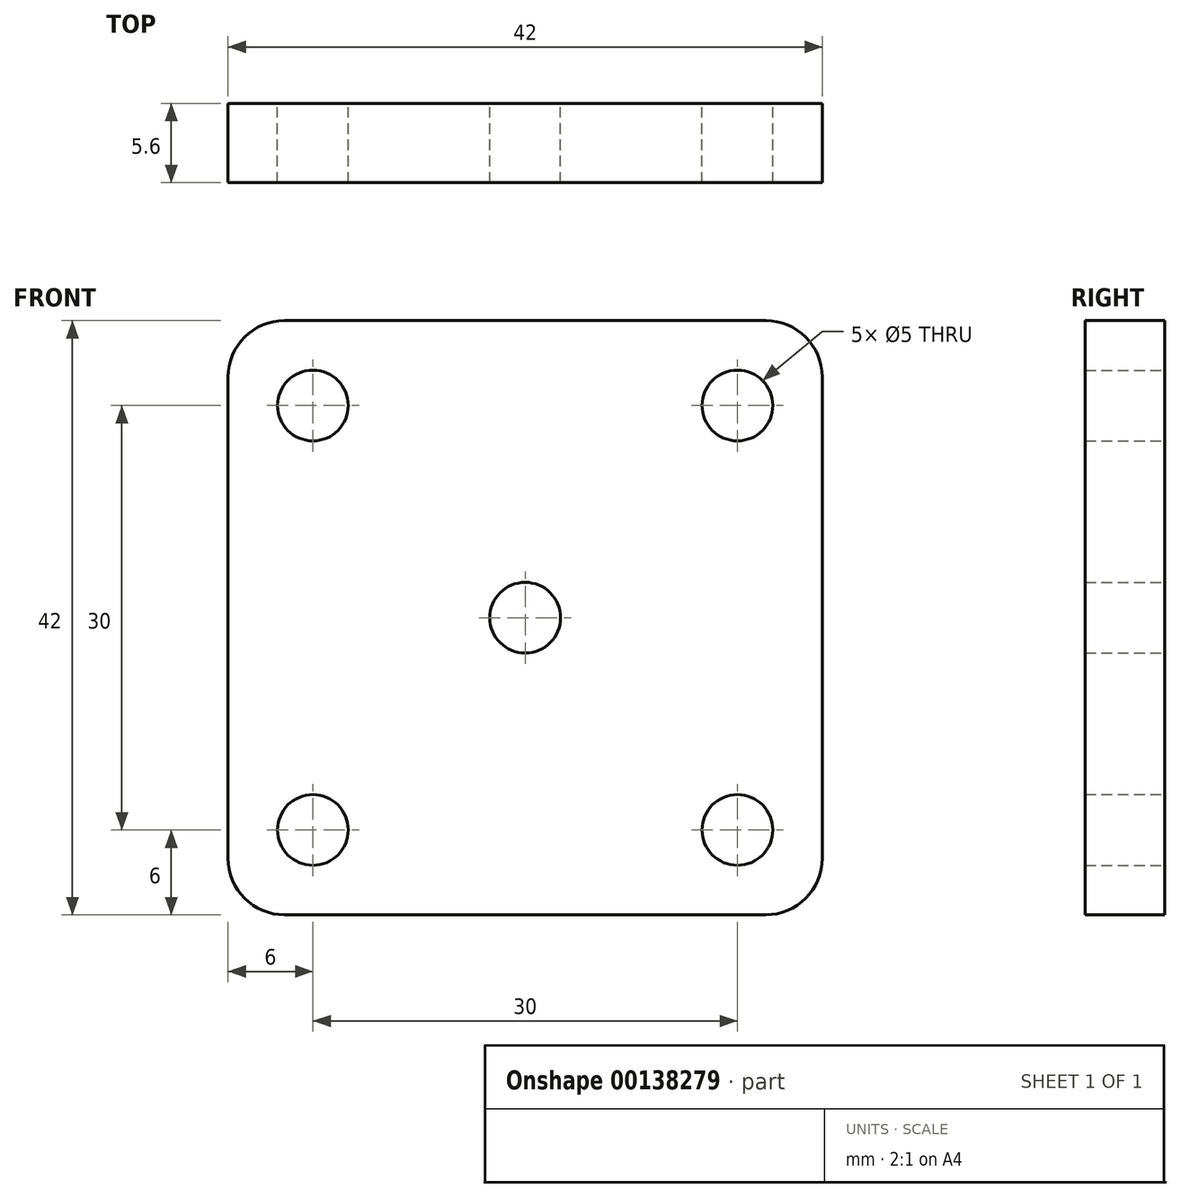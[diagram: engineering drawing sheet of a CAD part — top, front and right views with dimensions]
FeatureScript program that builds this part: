
annotation { "Feature Type Name" : "Feature", "Feature Type Description" : "" }
export const myFeature = defineFeature(function(context is Context, id is Id, definition is map)
    precondition{}
    {
        {
            var Q0;
            Q0=qCreatedBy(makeId("Front.planeOp"),FACE);
            var sketch = newSketch(context, id + "F0", { "sketchPlane" : qUnion([Q0])});
            skLineSegment(sketch, "E0.bottom", {"start": v(15, 15) * mm, "end": v(-15, 15) * mm, "construction": true});
            skLineSegment(sketch, "E0.top", {"start": v(15, -15) * mm, "end": v(-15, -15) * mm, "construction": true});
            skLineSegment(sketch, "E0.left", {"start": v(15, 15) * mm, "end": v(15, -15) * mm, "construction": true});
            skLineSegment(sketch, "E0.right", {"start": v(-15, 15) * mm, "end": v(-15, -15) * mm, "construction": true});
            skPoint(sketch, "E0.middle", {"position": v(0, 0) * mm});
            skCircle(sketch, "E1", {"center": v(-15, 15) * mm, "radius": 2.5 * mm});
            skCircle(sketch, "E2", {"center": v(15, 15) * mm, "radius": 2.5 * mm});
            skCircle(sketch, "E3", {"center": v(15, -15) * mm, "radius": 2.5 * mm});
            skCircle(sketch, "E4", {"center": v(-15, -15) * mm, "radius": 2.5 * mm});
            skLineSegment(sketch, "E5.bottom", {"start": v(17, 21) * mm, "end": v(-17, 21) * mm});
            skLineSegment(sketch, "E5.top", {"start": v(17, -21) * mm, "end": v(-17, -21) * mm});
            skLineSegment(sketch, "E5.left", {"start": v(21, 17) * mm, "end": v(21, -17) * mm});
            skLineSegment(sketch, "E5.right", {"start": v(-21, 17) * mm, "end": v(-21, -17) * mm});
            skCircle(sketch, "E6", {"center": v(-15, 15) * mm, "radius": 4 * mm, "construction": true});
            skCircle(sketch, "E7", {"center": v(0, 0) * mm, "radius": 2.5 * mm});
            skPoint(sketch, "E8.visualSharp", {"position": v(-21, 21) * mm});
            skArc(sketch, "E8.filletArc", {"start": v(-17, 21) * mm, "mid": v(-19.83, 19.83) * mm, "end": v(-21, 17) * mm});
            skPoint(sketch, "E9.visualSharp", {"position": v(21, 21) * mm});
            skArc(sketch, "E9.filletArc", {"start": v(21, 17) * mm, "mid": v(19.83, 19.83) * mm, "end": v(17, 21) * mm});
            skPoint(sketch, "E10.visualSharp", {"position": v(21, -21) * mm});
            skArc(sketch, "E10.filletArc", {"start": v(17, -21) * mm, "mid": v(19.83, -19.83) * mm, "end": v(21, -17) * mm});
            skPoint(sketch, "E11.visualSharp", {"position": v(-21, -21) * mm});
            skArc(sketch, "E11.filletArc", {"start": v(-21, -17) * mm, "mid": v(-19.83, -19.83) * mm, "end": v(-17, -21) * mm});
            skCircle(sketch, "E12", {"center": v(-15, 15) * mm, "radius": 5 * mm, "construction": true});
            skSolve(sketch);
        }
        {
            var Q0;
            Q0=makeQuery(id+"F0.imprint","IMPRINT",FACE,{"disambiguationData":[TD([[makeQuery(id+"F0.imprint","IMPRINT",EDGE,{"derivedFrom":sQuery(id+"F0.wireOp",EDGE,"E1")}),-1.0]])]});
            extrude(context, id + "F1", {"entities" : qUnion([Q0]), "depth" : 5.6 * mm});
        }
    });
